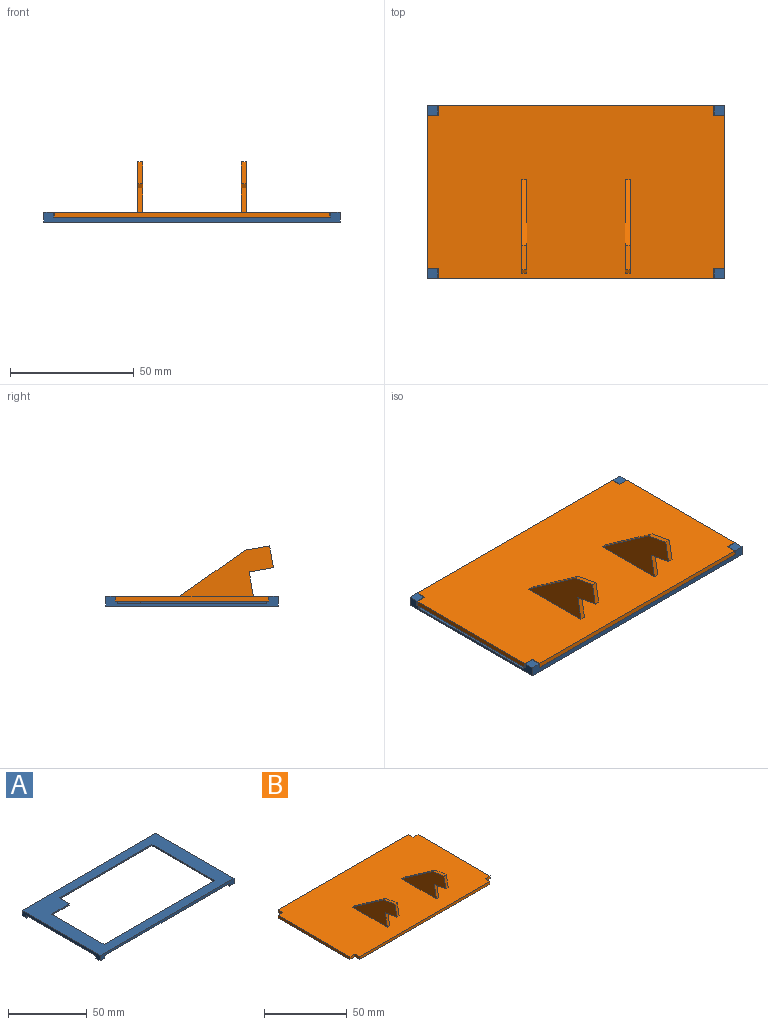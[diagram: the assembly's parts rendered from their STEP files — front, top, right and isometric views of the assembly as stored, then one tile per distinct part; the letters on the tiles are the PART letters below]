
ASSEMBLY  parts=2 mates=1
PART A: 30 faces, bbox 120x70x4 mm
  f0: plane 120x70mm, normal (0,0,-1), area 1790mm2, adj f7,f8,f9,f10,f13,f14,f15,f16
  f1: plane 9x1mm, normal (1,0,0), area 9mm2, adj f2,f6,f11,f12
  f2: plane 83x1mm, normal (0,-1,0), area 83mm2, adj f1,f3,f11,f12
  f3: plane 56x1mm, normal (-1,0,0), area 56mm2, adj f2,f4,f11,f12
  f4: plane 99x1mm, normal (0,1,0), area 99mm2, adj f3,f5,f11,f12
  f5: plane 47x1mm, normal (1,0,0), area 47mm2, adj f4,f6,f11,f12
  f6: plane 16x1mm, normal (0,-1,0), area 16mm2, adj f1,f5,f11,f12
  f7: plane 70x4mm, normal (1,0,0), area 96mm2, adj f0,f8,f10,f11,f12,f13,f17,f24
  f8: plane 120x4mm, normal (0,1,0), area 256mm2, adj f0,f7,f9,f11,f21,f23,f28,f29
  f9: plane 70x4mm, normal (-1,0,0), area 156mm2, adj f0,f8,f10,f11,f18,f20,f22,f23
  f10: plane 120x4mm, normal (0,-1,0), area 256mm2, adj f0,f7,f9,f11,f19,f20,f25,f26
  f11: plane 120x70mm, normal (0,0,1), area 3000mm2, adj f1,f2,f3,f4,f5,f6,f7,f8
  f12: plane 111.5x60mm, normal (0,0,-1), area 1146mm2, adj f1,f2,f3,f4,f5,f6,f7,f13
  f13: plane 111.5x1mm, normal (0,1,0), area 111.5mm2, adj f0,f7,f12,f14
  f14: plane 51x1mm, normal (1,0,0), area 51mm2, adj f0,f12,f13,f15
  f15: plane 16x1mm, normal (0,-1,0), area 16mm2, adj f0,f12,f14,f16
  f16: plane 9x1mm, normal (1,0,0), area 9mm2, adj f0,f12,f15,f17
  f17: plane 95.5x1mm, normal (0,-1,0), area 95.5mm2, adj f0,f7,f12,f16
  f18: plane 4x2mm, normal (0,1,0), area 8mm2, adj f0,f9,f19,f20
  f19: plane 4x2mm, normal (1,0,0), area 8mm2, adj f0,f10,f18,f20
  f20: plane 4x4mm, normal (0,0,-1), area 16mm2, adj f9,f10,f18,f19
  f21: plane 4x2mm, normal (1,0,0), area 8mm2, adj f0,f8,f22,f23
  f22: plane 4x2mm, normal (0,-1,0), area 8mm2, adj f0,f9,f21,f23
  f23: plane 4x4mm, normal (0,0,-1), area 16mm2, adj f8,f9,f21,f22
  f24: plane 4x2mm, normal (0,1,0), area 8mm2, adj f0,f7,f25,f26
  f25: plane 4x2mm, normal (-1,0,0), area 8mm2, adj f0,f10,f24,f26
  f26: plane 4x4mm, normal (0,0,-1), area 16mm2, adj f7,f10,f24,f25
  f27: plane 4x2mm, normal (0,-1,0), area 8mm2, adj f0,f7,f28,f29
  f28: plane 4x2mm, normal (-1,0,0), area 8mm2, adj f0,f8,f27,f29
  f29: plane 4x4mm, normal (0,0,-1), area 16mm2, adj f7,f8,f27,f28
PART B: 28 faces, bbox 120x70x22.4 mm
  f0: plane 37.96x20.39mm, normal (1,0,0), area 367.8mm2, adj f3,f23,f24,f25,f26,f27
  f1: plane 37.96x20.39mm, normal (-1,0,0), area 367.8mm2, adj f3,f18,f19,f20,f21,f22
  f2: plane 37.96x20.39mm, normal (1,0,0), area 367.8mm2, adj f3,f18,f19,f20,f21,f22
  f3: plane 120x70mm, normal (0,0,1), area 8210.1mm2, adj f0,f1,f2,f4,f5,f6,f7,f8
  f4: plane 4.2x2mm, normal (0,1,0), area 8.4mm2, adj f3,f5,f15,f16
  f5: plane 61.6x2mm, normal (-1,0,0), area 123.2mm2, adj f3,f4,f6,f16
  f6: plane 4.2x2mm, normal (0,-1,0), area 8.4mm2, adj f3,f5,f7,f16
  f7: plane 4.2x2mm, normal (-1,0,0), area 8.4mm2, adj f3,f6,f8,f16
  f8: plane 111.6x2mm, normal (0,-1,0), area 223.2mm2, adj f3,f7,f9,f16
  f9: plane 4.2x2mm, normal (1,0,0), area 8.4mm2, adj f3,f8,f10,f16
  f10: plane 4.2x2mm, normal (0,-1,0), area 8.4mm2, adj f3,f9,f11,f16
  f11: plane 61.6x2mm, normal (1,0,0), area 123.2mm2, adj f3,f10,f12,f16
  f12: plane 4.2x2mm, normal (0,1,0), area 8.4mm2, adj f3,f11,f13,f16
  f13: plane 4.2x2mm, normal (1,0,0), area 8.4mm2, adj f3,f12,f14,f16
  f14: plane 111.6x2mm, normal (0,1,0), area 223.2mm2, adj f3,f13,f15,f16
  f15: plane 4.2x2mm, normal (-1,0,0), area 8.4mm2, adj f3,f4,f14,f16
  f16: plane 120x70mm, normal (0,0,-1), area 8329.4mm2, adj f4,f5,f6,f7,f8,f9,f10,f11
  f17: plane 37.96x20.39mm, normal (-1,0,0), area 367.8mm2, adj f3,f23,f24,f25,f26,f27
  f18: plane 9.85x2mm, normal (0,-0.17,-0.98), area 20mm2, adj f1,f2,f19,f22
  f19: plane 8.81x2mm, normal (0,-0.98,0.17), area 17.9mm2, adj f1,f2,f18,f20
  f20: plane 9.85x2mm, normal (0,0.17,0.98), area 20mm2, adj f1,f2,f19,f21
  f21: plane 26.56x18.65mm, normal (0,0.57,0.82), area 64.9mm2, adj f1,f2,f3,f20
  f22: plane 9.85x2mm, normal (0,-0.98,0.17), area 20mm2, adj f1,f2,f3,f18
  f23: plane 9.85x2mm, normal (0,-0.98,0.17), area 20mm2, adj f0,f3,f17,f27
  f24: plane 26.56x18.65mm, normal (0,0.57,0.82), area 64.9mm2, adj f0,f3,f17,f25
  f25: plane 9.85x2mm, normal (0,0.17,0.98), area 20mm2, adj f0,f17,f24,f26
  f26: plane 8.81x2mm, normal (0,-0.98,0.17), area 17.9mm2, adj f0,f17,f25,f27
  f27: plane 9.85x2mm, normal (0,-0.17,-0.98), area 20mm2, adj f0,f17,f23,f26
PLACE A rot(axis=(0,1,0),180deg) t=(65.23,0.29,8.5)mm
PLACE B t=(-30.27,-4.71,8.5)mm
MATE fastened A.f0 <-> B.f16  axis (0,0,1) through (29.73,-4.71,8.5)mm
